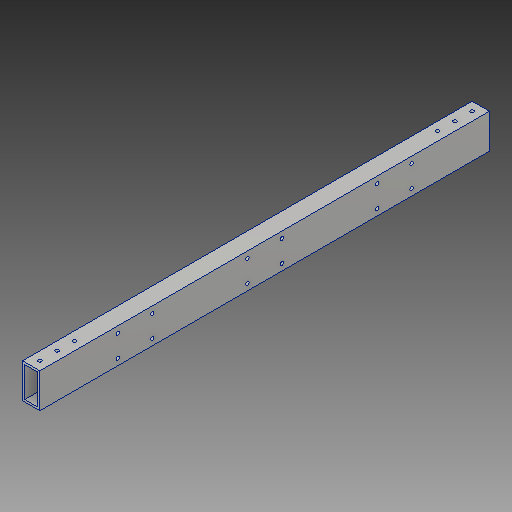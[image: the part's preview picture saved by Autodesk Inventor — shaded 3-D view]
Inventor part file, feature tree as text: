
AUTODESK INVENTOR PART (.ipt)
format: ipt  version: 2018 (Build 220112000, 112)  size: 176,640 bytes
history: native  units: in
note: dims shown in document units (in); Inventor stores cm internally (conversion verified against a paired STEP export)
features: extrude x5, sketch x5
ambient origin geometry x8: Origin, YZ Plane, XZ Plane, XY Plane, X Axis, Y Axis, Z Axis, Center Point
bodies: Solid1 (feature_tree)
feature tree (10):
  extrude  "Extrusion1"  Depth=2.0in
  extrude  "Extrusion2"  Depth=0.125in
  extrude  "Extrusion3"  Depth=0.125in
  extrude  "Extrusion4"  Depth=26.0in
  extrude  "Extrusion5"  Depth=1.0in
  sketch  "Sketch1"  dims[d0=1.0in d1=2.0in]
  sketch  "Sketch2"  dims[d2=0.125in d3=0.125in]
  sketch  "Sketch3"  dims[d4=0.125in d5=0.125in]
  sketch  "Sketch4"  dims[d6=26.0in d7=0.0in d8=0.5in]
  sketch  "Sketch5"  dims[d9=1.0in d10=1.0in d11=0.2in d12=0.5in d13=1.0in d14=1.0in d15=26.0in d16=0.0in d17=4.5in d18=2.0in d19=0.375in d20=0.2in d21=0.375in d22=26.0in d23=0.0in d24=5.5in d25=2.0in d26=26.0in d27=0.0in d28=5.5in d29=2.0in d30=26.0in d31=0.0in]
